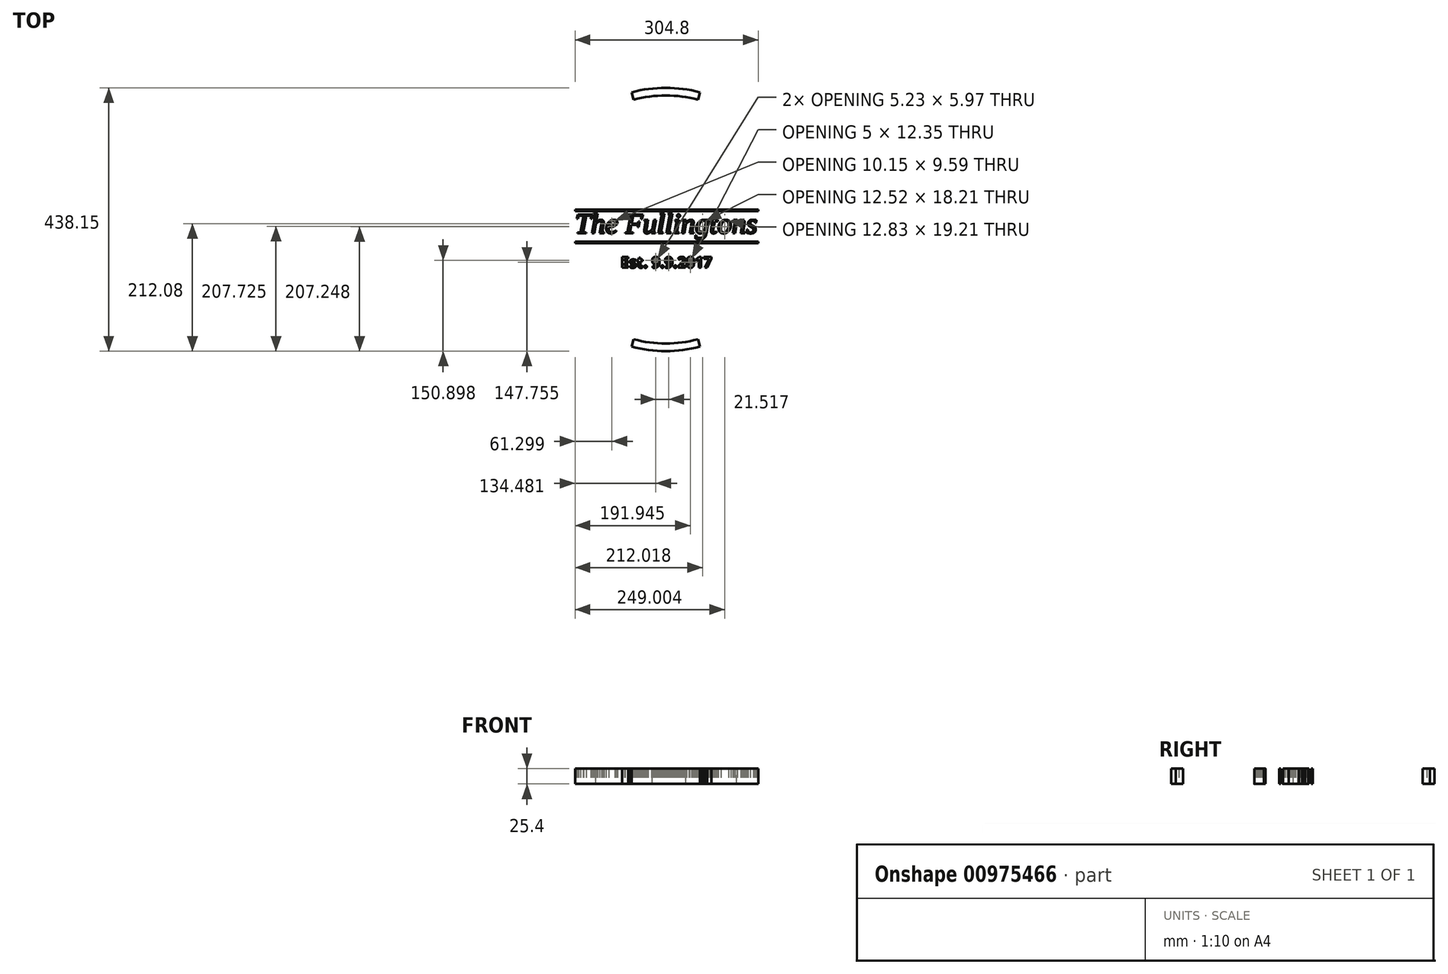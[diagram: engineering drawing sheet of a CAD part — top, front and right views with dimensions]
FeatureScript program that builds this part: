
annotation { "Feature Type Name" : "Feature", "Feature Type Description" : "" }
export const myFeature = defineFeature(function(context is Context, id is Id, definition is map)
    precondition{}
    {
        {
            var Q0;
            Q0=qCreatedBy(makeId("Top.planeOp"),FACE);
            var sketch = newSketch(context, id + "F0", { "sketchPlane" : qUnion([Q0])});
            skText(sketch, "E0", { "text": "The Fullingtons", "fontName": "Tinos-Italic.ttf"});
            skLineSegment(sketch, "E1.bottom", {"start": v(0, 0) * mm, "end": v(304.8, 0) * mm});
            skLineSegment(sketch, "E1.top", {"start": v(0, 2.54) * mm, "end": v(304.8, 2.54) * mm});
            skLineSegment(sketch, "E1.left", {"start": v(0, 0) * mm, "end": v(0, 2.54) * mm});
            skLineSegment(sketch, "E1.right", {"start": v(304.8, 0) * mm, "end": v(304.8, 2.54) * mm});
            skLineSegment(sketch, "E2.bottom", {"start": v(0, -50.8) * mm, "end": v(304.8, -50.8) * mm});
            skLineSegment(sketch, "E2.top", {"start": v(0, -53.34) * mm, "end": v(304.8, -53.34) * mm});
            skLineSegment(sketch, "E2.left", {"start": v(0, -50.8) * mm, "end": v(0, -53.34) * mm});
            skLineSegment(sketch, "E2.right", {"start": v(304.8, -50.8) * mm, "end": v(304.8, -53.34) * mm});
            const initialGuessF0  = {"E0": [0, -0.03687, 1, 0, 0.03433]};
            skSetInitialGuess(sketch, initialGuessF0);
            skSolve(sketch);
        }
        {
            var Q0;
            Q0=qCreatedBy(makeId("Top.planeOp"),FACE);
            var sketch = newSketch(context, id + "F1", { "sketchPlane" : qUnion([Q0])});
            skCircle(sketch, "E3", {"center": v(152.4, -15.24) * mm, "radius": 254 * mm});
            skCircle(sketch, "E4", {"center": v(152.4, -15.24) * mm, "radius": 266.7 * mm});
            skSolve(sketch);
        }
        {
            var Q0;
            Q0 = qSketchRegion(id + "F0", true);
            extrude(context, id + "F2", {"entities" : qUnion([Q0]), "depth" : 25.4 * mm, "offsetDistance" : 25.4 * mm});
        }
        {
            var Q0;
            Q0=qCreatedBy(makeId("Top.planeOp"),FACE);
            var sketch = newSketch(context, id + "F3", { "sketchPlane" : qUnion([Q0])});
            skText(sketch, "E5", { "text": "Est. 9.9.2017", "fontName": "OpenSans-Bold.ttf"});
            const initialGuessF3  = {"E5": [0.0762, -0.0943, 1, 0, 0.0181]};
            skSetInitialGuess(sketch, initialGuessF3);
            skSolve(sketch);
        }
        {
            var Q0;
            Q0 = qSketchRegion(id + "F3", true);
            extrude(context, id + "F4", {"entities" : qUnion([Q0]), "depth" : 25.4 * mm, "offsetDistance" : 25.4 * mm});
        }
        {
            var Q0;
            Q0=makeQuery(id+"F1.imprint","IMPRINT",FACE,{"disambiguationData":[TD([[makeQuery(id+"F1.imprint","IMPRINT",EDGE,{"derivedFrom":sQuery(id+"F1.wireOp",EDGE,"E3")}),1.0]])]});
            var sketch = newSketch(context, id + "F5", { "sketchPlane" : qUnion([Q0])});
            skLineSegment(sketch, "E6", {"start": v(204.39, 185.35) * mm, "end": v(207.67, 197.62) * mm});
            skLineSegment(sketch, "E7", {"start": v(150.97, -14) * mm, "end": v(150.97, 217.26) * mm, "construction": true});
            skLineSegment(sketch, "E8", {"start": v(97.56, 185.35) * mm, "end": v(94.27, 197.62) * mm});
            skArc(sketch, "E9", {"start": v(207.67, 197.62) * mm, "mid": v(150.97, 205.08) * mm, "end": v(94.27, 197.62) * mm});
            skArc(sketch, "E10", {"start": v(204.39, 185.35) * mm, "mid": v(150.97, 192.38) * mm, "end": v(97.56, 185.35) * mm});
            skLineSegment(sketch, "E11", {"start": v(150.97, -14) * mm, "end": v(477.46, -14) * mm, "construction": true});
            skLineSegment(sketch, "E12.MirrorCS", {"start": v(204.39, -213.33) * mm, "end": v(207.67, -225.6) * mm});
            skLineSegment(sketch, "E13.MirrorCS", {"start": v(97.56, -213.33) * mm, "end": v(94.27, -225.6) * mm});
            skArc(sketch, "E14.MirrorCS", {"start": v(204.39, -213.33) * mm, "mid": v(150.97, -220.37) * mm, "end": v(97.56, -213.33) * mm});
            skArc(sketch, "E15.MirrorCS", {"start": v(207.67, -225.6) * mm, "mid": v(150.97, -233.07) * mm, "end": v(94.27, -225.6) * mm});
            skSolve(sketch);
        }
        {
            var Q0;
            Q0 = qSketchRegion(id + "F5", true);
            extrude(context, id + "F6", {"entities" : qUnion([Q0]), "depth" : 25.4 * mm, "offsetDistance" : 25.4 * mm});
        }
    });
